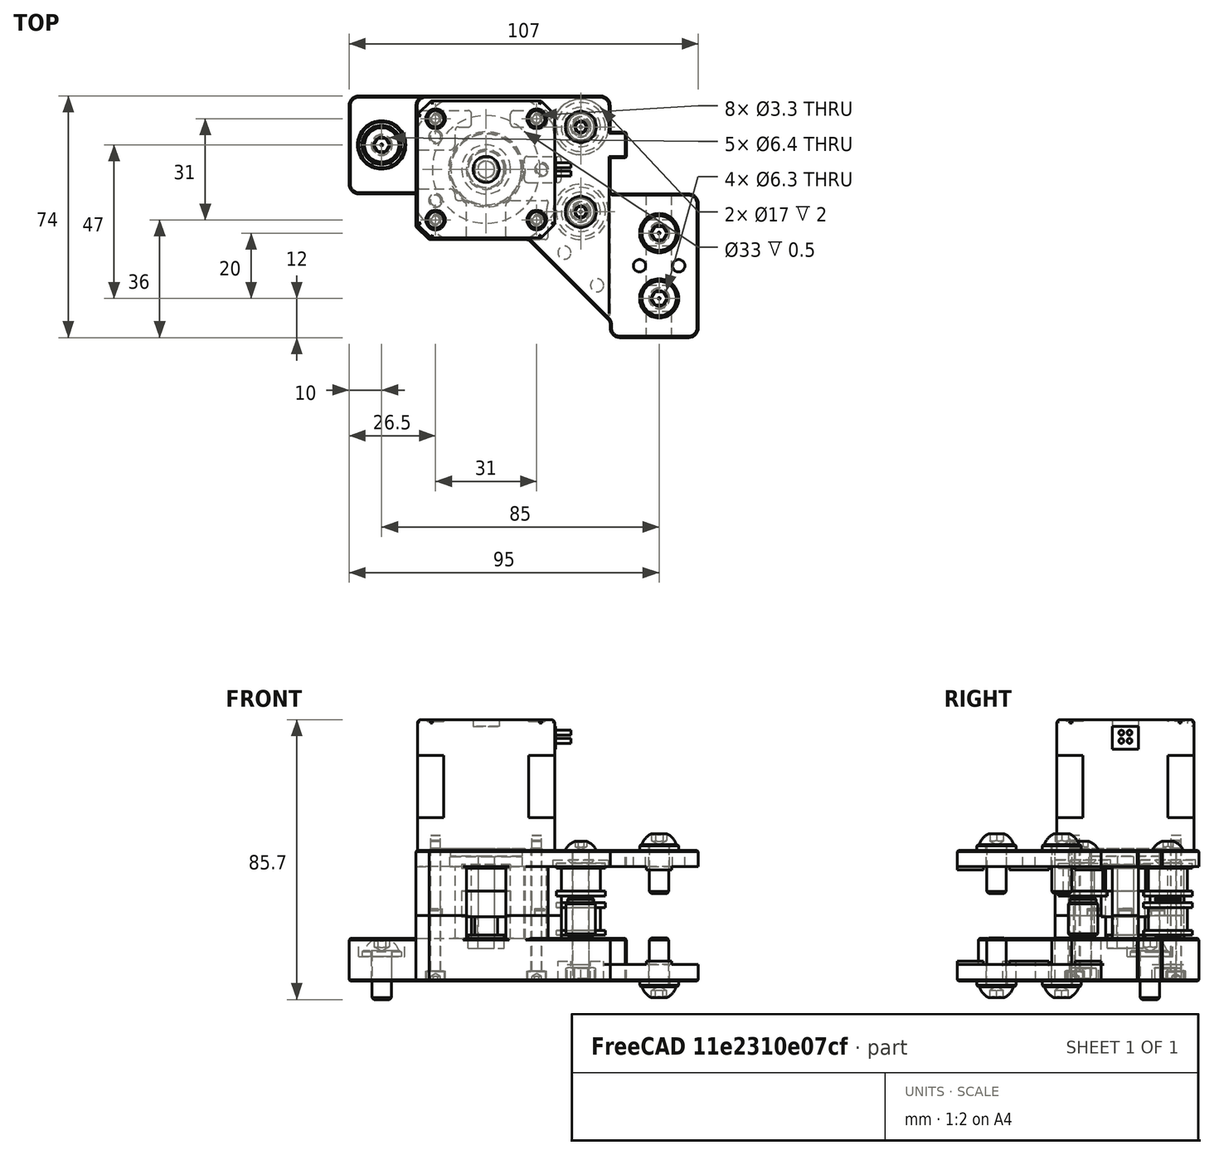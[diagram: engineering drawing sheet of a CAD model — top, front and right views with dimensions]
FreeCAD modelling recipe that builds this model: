
FCSTD DOCUMENT  (FreeCAD 0.19R24291 (Git))
Label: right-motor-assembly
License: Other
LicenseURL: GPL3
objects: Part::FeaturePython×18, Part::Feature×11, App::Part×1
note: 29 computed .brp shape members not serialized (recipe doc carries the construction recipe); baked Part::Feature solids carry a one-line shape summary decoded from their .brp

FEATURE [Part::Feature] Part__Mirroring009001  label="pulley-spacer001"
  shape: bbox 6.9 x 6.9 x 5.5 mm, 4 faces (baked)
FEATURE [Part::Feature] Part__Mirroring008001  label="MR115ZZ"
  shape: bbox 11 x 11 x 4 mm, 4 faces (baked)
FEATURE [Part::Feature] Part__Mirroring007001  label="20t-pulley001"
  shape: bbox 15 x 15 x 16 mm, 8 faces (baked)
FEATURE [Part::Feature] Part__Mirroring005001  label="dummy-idler"
  Placement = pos=(2,0,0) rot=(0,0,1;0rad)
  shape: bbox 9 x 9 x 11.85 mm, 9 faces (baked)
FEATURE [Part::Feature] Part__Mirroring003001  label="smooth-idler-6mm007"
  Placement = pos=(2,0,0) rot=(0,0,1;0rad)
  shape: bbox 15 x 15 x 10 mm, 8 faces (baked)
FEATURE [Part::Feature] Part__Mirroring002001  label="smooth-idler-6mm004"
  Placement = pos=(2,0,0) rot=(0,0,1;0rad)
  shape: bbox 15 x 15 x 10 mm, 8 faces (baked)
FEATURE [Part::Feature] Part__Mirroring001001  label="smooth-idler-6mm"
  Placement = pos=(2,0,0) rot=(0,0,1;0rad)
  shape: bbox 15 x 15 x 10 mm, 8 faces (baked)
FEATURE [Part::Feature] Part__Mirroring009002  label="motor-40mm"
  Placement = pos=(-15.5,-60.5,0) rot=(0,0,-1;1.5708rad)
  shape: bbox 47 x 42 x 67 mm, 100 faces (baked)
FEATURE [Part::Feature] Cut002001  label="spacer"
  Placement = pos=(-9,-9.5,20) rot=(0,0,1;0rad)
  shape: bbox 8 x 8 x 1.7 mm, 5 faces (baked)
FEATURE [Part::FeaturePython] Washer  label="M6-Washer"  # Fasteners workbench fastener (typed FeaturePython)
  Placement = pos=(15,-62,35) rot=(0,0,1;0rad)
  diameter = 2
  invert = true
  matchOuter = true
  offset = 0
  type = 4
FEATURE [Part::FeaturePython] Washer001  label="M6-Washer009"  # Fasteners workbench fastener (typed FeaturePython)
  Placement = pos=(15,-42,35) rot=(0,0,1;0rad)
  diameter = 2
  invert = true
  matchOuter = true
  offset = 0
  type = 4
FEATURE [Part::FeaturePython] Washer002  label="M6-Washer008"  # Fasteners workbench fastener (typed FeaturePython)
  Placement = pos=(15,-62,-5) rot=(1,0,0;3.14159rad)
  diameter = 2
  invert = false
  matchOuter = true
  offset = 0
  type = 4
FEATURE [Part::FeaturePython] Washer003  label="M6-Washer007"  # Fasteners workbench fastener (typed FeaturePython)
  Placement = pos=(15,-42,-5) rot=(1,0,0;3.14159rad)
  diameter = 2
  invert = false
  matchOuter = true
  offset = 0
  type = 4
FEATURE [Part::FeaturePython] Washer004  label="M6-Washer006"  # Fasteners workbench fastener (typed FeaturePython)
  Placement = pos=(-70,-15,2.5) rot=(0,0,1;0rad)
  diameter = 2
  invert = true
  matchOuter = true
  offset = 0
  type = 4
FEATURE [Part::FeaturePython] Screw  label="M6x15-Screw"  # Fasteners workbench fastener (typed FeaturePython)
  Placement = pos=(-70,-15,4.3) rot=(0,0,1;0rad)
  baseObject = -> Washer004 [Edge1]
  diameter = 4
  invert = false
  length = 13
  lengthCustom = 15
  matchOuter = true
  offset = 0
  thread = false
  type = 39
FEATURE [Part::FeaturePython] Screw001  label="M6x15-Screw002"  # Fasteners workbench fastener (typed FeaturePython)
  Placement = pos=(15,-42,36.8) rot=(0,0,1;0rad)
  baseObject = -> Washer001 [Edge1]
  diameter = 4
  invert = false
  length = 13
  lengthCustom = 15
  matchOuter = true
  offset = 0
  thread = false
  type = 39
FEATURE [Part::FeaturePython] Screw002  label="M6x15-Screw001"  # Fasteners workbench fastener (typed FeaturePython)
  Placement = pos=(15,-62,36.8) rot=(0,0,1;0rad)
  baseObject = -> Washer [Edge1]
  diameter = 4
  invert = false
  length = 13
  lengthCustom = 15
  matchOuter = true
  offset = 0
  thread = false
  type = 39
FEATURE [Part::FeaturePython] Screw003  label="M6x15-Screw004"  # Fasteners workbench fastener (typed FeaturePython)
  Placement = pos=(15,-62,-6.8) rot=(-1,0,0;3.14159rad)
  baseObject = -> Washer002 [Edge1]
  diameter = 4
  invert = false
  length = 13
  lengthCustom = 15
  matchOuter = true
  offset = 0
  thread = false
  type = 39
FEATURE [Part::FeaturePython] Screw004  label="M6x15-Screw003"  # Fasteners workbench fastener (typed FeaturePython)
  Placement = pos=(15,-42,-6.8) rot=(-1,0,0;3.14159rad)
  baseObject = -> Washer003 [Edge1]
  diameter = 4
  invert = false
  length = 13
  lengthCustom = 15
  matchOuter = true
  offset = 0
  thread = false
  type = 39
FEATURE [Part::FeaturePython] Screw005  label="M5x40-Screw"  # Fasteners workbench fastener (typed FeaturePython)
  Placement = pos=(-9,-35.5,35) rot=(0,0,1;0rad)
  diameter = 3
  invert = true
  length = 12
  lengthCustom = 40
  matchOuter = true
  offset = 0
  thread = false
  type = 39
FEATURE [Part::FeaturePython] Screw006  label="M5x40-Screw001"  # Fasteners workbench fastener (typed FeaturePython)
  Placement = pos=(-9,-9.5,35) rot=(0,0,1;0rad)
  diameter = 3
  invert = true
  length = 12
  lengthCustom = 40
  matchOuter = true
  offset = 0
  thread = false
  type = 39
FEATURE [Part::FeaturePython] Nut  label="M5-Nut"  # Fasteners workbench fastener (typed FeaturePython)
  Placement = pos=(-9,-35.5,-1) rot=(1,0,0;3.14159rad)
  diameter = 7
  invert = false
  matchOuter = true
  offset = 0
  thread = false
  type = 7
FEATURE [Part::FeaturePython] Nut001  label="M5-Nut001"  # Fasteners workbench fastener (typed FeaturePython)
  Placement = pos=(-9,-9.5,-1) rot=(1,0,0;3.14159rad)
  diameter = 7
  invert = false
  matchOuter = true
  offset = 0
  thread = false
  type = 7
FEATURE [Part::FeaturePython] Screw007  label="M3x40-Screw"  # Fasteners workbench fastener (typed FeaturePython)
  Placement = pos=(-22.5,-38,-2) rot=(1,0,0;3.14159rad)
  diameter = 4
  invert = false
  length = 10
  lengthCustom = 40
  matchOuter = true
  offset = 0
  thread = false
  type = 33
FEATURE [Part::FeaturePython] Screw008  label="M3x40-Screw005"  # Fasteners workbench fastener (typed FeaturePython)
  Placement = pos=(-53.5,-38,-2) rot=(1,0,0;3.14159rad)
  diameter = 4
  invert = false
  length = 10
  lengthCustom = 40
  matchOuter = true
  offset = 0
  thread = false
  type = 33
FEATURE [Part::FeaturePython] Screw009  label="M3x40-Screw004"  # Fasteners workbench fastener (typed FeaturePython)
  Placement = pos=(-53.5,-7,-2) rot=(1,0,0;3.14159rad)
  diameter = 4
  invert = false
  length = 10
  lengthCustom = 40
  matchOuter = true
  offset = 0
  thread = false
  type = 33
FEATURE [Part::FeaturePython] Screw010  label="M3x40-Screw003"  # Fasteners workbench fastener (typed FeaturePython)
  Placement = pos=(-22.5,-7,-2) rot=(1,0,0;3.14159rad)
  diameter = 4
  invert = false
  length = 10
  lengthCustom = 40
  matchOuter = true
  offset = 0
  thread = false
  type = 33
FEATURE [Part::Feature] Part__Mirroring009003005  label="Chamfer041001 (Mirror #1)001"
  Placement = pos=(0,-30,0) rot=(0,0,1;0rad)
  shape: bbox 86.5 x 74 x 20 mm, 149 faces (baked)
FEATURE [Part::Feature] Part__Mirroring009003004001  label="Chamfer042001 (Mirror #2)001"
  Placement = pos=(0,-30,0) rot=(0,0,1;0rad)
  shape: bbox 107 x 74 x 22 mm, 215 faces (baked)
FEATURE [App::Part] Part  label="right-motor-mount"
  Group = -> [Part__Mirroring009001,Part__Mirroring008001,Part__Mirroring007001,Part__Mirroring005001,Part__Mirroring003001,Part__Mirroring002001,Part__Mirroring001001,Part__Mirroring009002,Cut002001,Screw002,Screw005,Screw001,Washer001,Screw006,Washer,Screw,Screw004,Nut001,Screw010,Screw007,Screw003,Washer003,Screw009,Washer004,Screw008,Nut,Washer002,Part__Mirroring009003005,Part__Mirroring009003004001]
  Origin = -> Origin
